# Revit family: Zumtobel SCENO 2x7
name_source: partatom
category: Lighting Fixtures
revit_build: Autodesk Revit 2018 (Build: 20170223_1515(x64)
units: mm (PartAtom-declared; Revit-internal decimal feet)

## family parameters
Cut with Voids When Loaded = No
Host = Face
Light Source = Yes
OmniClass Number = 23.80.70.11
OmniClass Title = Luminaries for Internal Lighting
Part Type = Normal
Room Calculation Point = No
Round Connector Dimension = Use Diameter
Shared = No

## types (1)
- SCENO 2X7 2000-930 SWI TEC VFL BK
    Apparent Load = 17 VA
    Assembly Code = D5020200
    Body = Zumtobel_Metal_Black
    Color Filter = 16777215
    Default Elevation = 0 mm  [stored 0 ft]
    Depth = 143 mm
    Description = LED Spot luminaire
    Dimming Lamp Color Temperature Shift = <None>
    Emit Shape Visible in Rendering = No
    Emit from Rectangle Length = 286 mm
    Emit from Rectangle Width = 143 mm
    Height = 105 mm  [stored 0.344488 ft]
    Length = 286 mm
    Manufacturer = Zumtobel Lighting
    Model = 42949785
    Photometric Web File = 42949785_(WNG-Flügel_LEO1).IES
    Tilt Angle = -90.00°
    URL = http://www.zumtobel.com
    Voltage = 230 V

note: [stored X ft] marks values corroborated as IEEE doubles in the binary element streams (Revit-internal decimal feet)

## geometry (parser evidence)
native form markers: Sweep x3
no freeform markers — native parametric forms only
